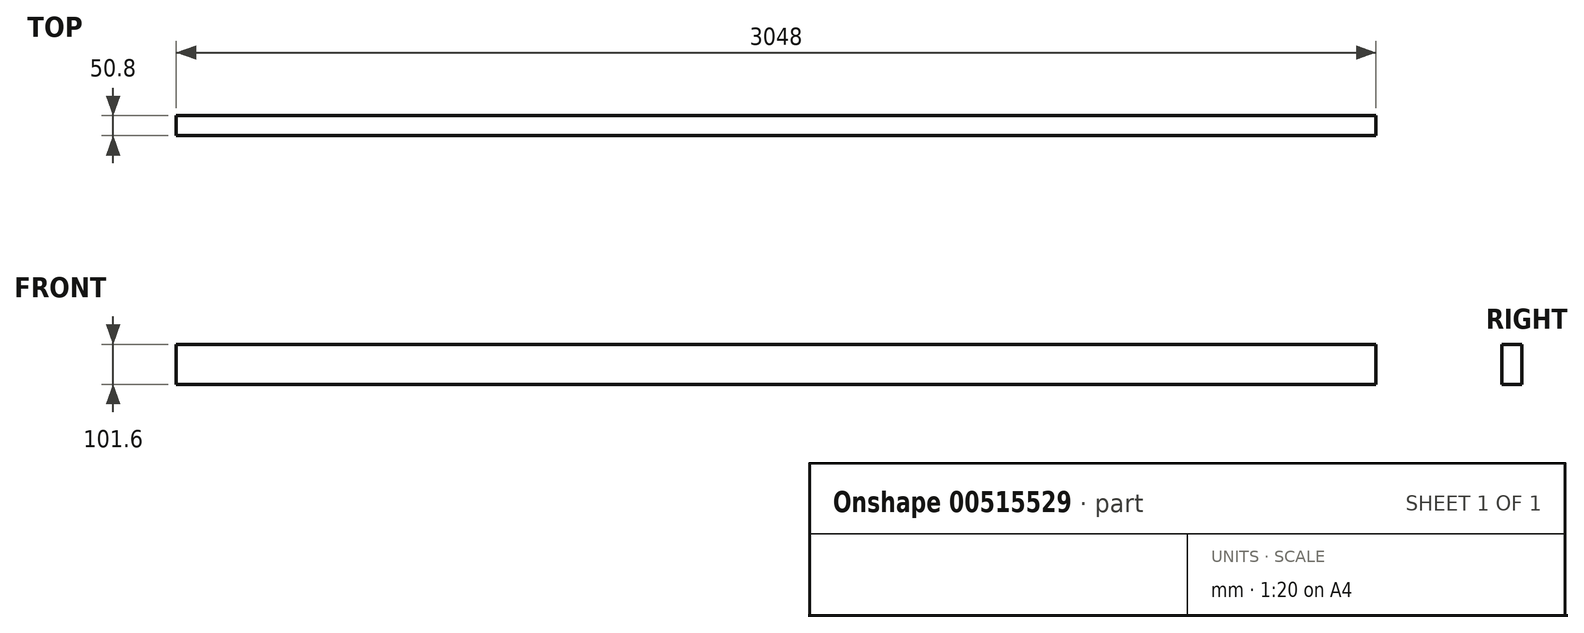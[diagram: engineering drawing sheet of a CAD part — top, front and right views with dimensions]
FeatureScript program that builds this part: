
annotation { "Feature Type Name" : "Feature", "Feature Type Description" : "" }
export const myFeature = defineFeature(function(context is Context, id is Id, definition is map)
    precondition{}
    {
        {
            var Q0;
            Q0=qCreatedBy(makeId("Right.planeOp"),FACE);
            var sketch = newSketch(context, id + "F0", { "sketchPlane" : qUnion([Q0])});
            skLineSegment(sketch, "E0.bottom", {"start": v(25.4, -50.8) * mm, "end": v(-25.4, -50.8) * mm});
            skLineSegment(sketch, "E0.top", {"start": v(25.4, 50.8) * mm, "end": v(-25.4, 50.8) * mm});
            skLineSegment(sketch, "E0.left", {"start": v(25.4, -50.8) * mm, "end": v(25.4, 50.8) * mm});
            skLineSegment(sketch, "E0.right", {"start": v(-25.4, -50.8) * mm, "end": v(-25.4, 50.8) * mm});
            skPoint(sketch, "E0.middle", {"position": v(0, 0) * mm});
            skSolve(sketch);
        }
        {
            var Q0;
            Q0=makeQuery(id+"F0.imprint","IMPRINT",FACE,{"disambiguationData":[TD([[makeQuery(id+"F0.imprint","IMPRINT",EDGE,{"derivedFrom":sQuery(id+"F0.wireOp",EDGE,"E0.bottom")}),-1.0]])]});
            extrude(context, id + "F1", {"entities" : qUnion([Q0]), "endBound" : BoundingType.SYMMETRIC, "depth" : 3048 * mm, "offsetDistance" : 25.4 * mm});
        }
    });
